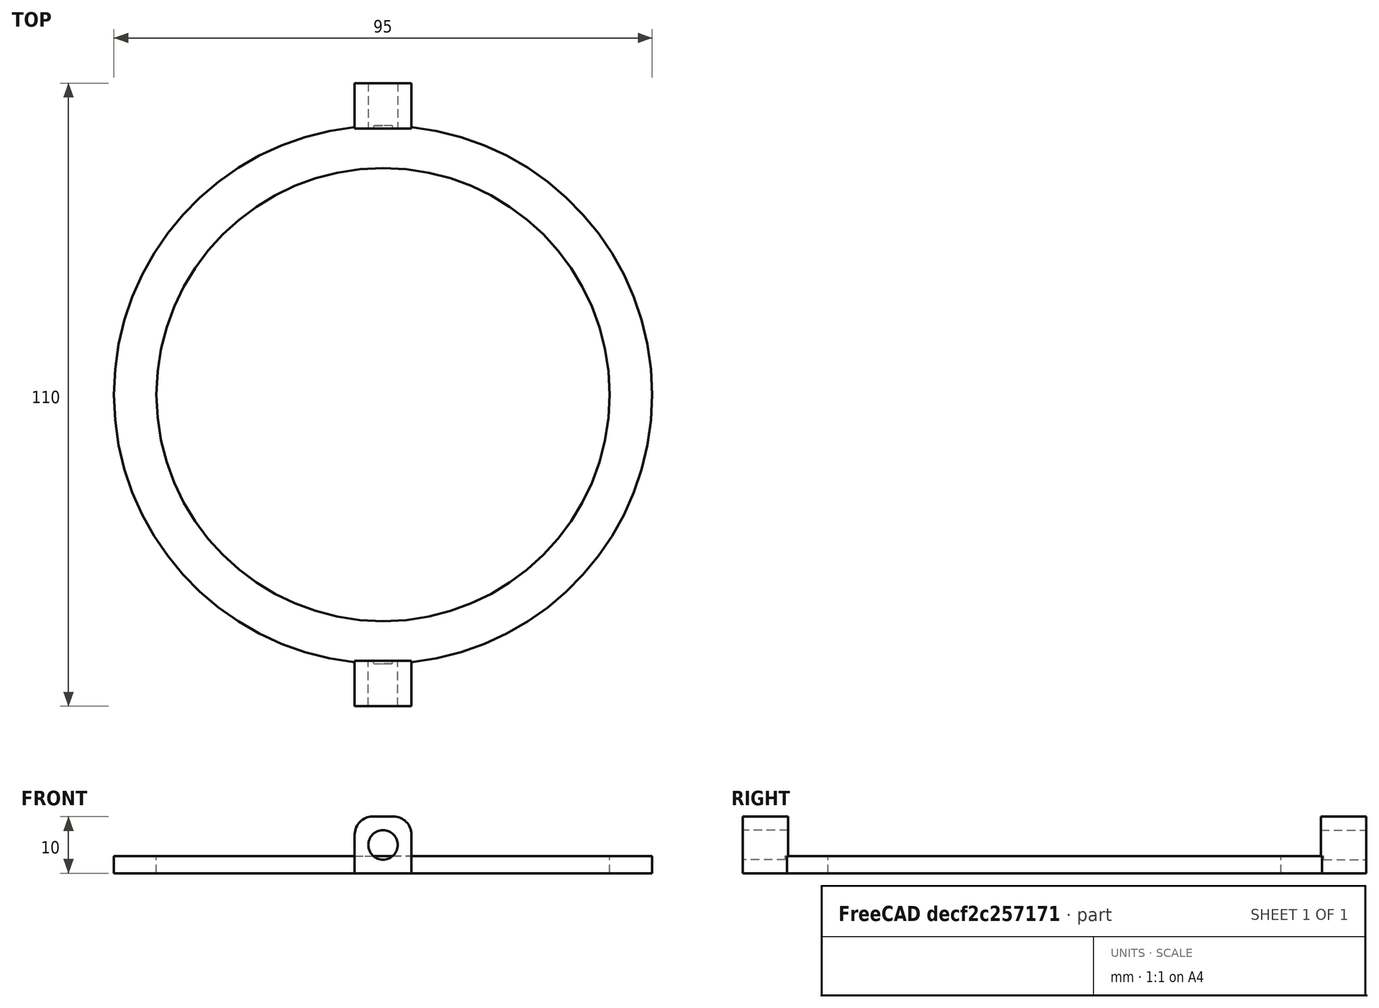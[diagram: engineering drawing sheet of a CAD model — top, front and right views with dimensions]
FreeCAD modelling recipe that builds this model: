
FCSTD DOCUMENT  (FreeCAD 0.19R24291 (Git))
Label: ring
License: All rights reserved
LicenseURL: http://en.wikipedia.org/wiki/All_rights_reserved
objects: Sketcher::SketchObject×2, PartDesign::Pad×2, PartDesign::Mirrored×2, Mesh::Feature×1, PartDesign::MultiTransform×1, PartDesign::Body×1
note: 10 computed .brp shape members not serialized (recipe doc carries the construction recipe); baked Part::Feature solids carry a one-line shape summary decoded from their .brp

FEATURE [Mesh::Feature] RING
FEATURE [Sketcher::SketchObject] Sketch
  FullyConstrained = true
  MapMode = 5
  Support = -> [XY_Plane]
  sketch-geometry (4):
    g0: ArcOfCircle CenterX=0 CenterY=0 CenterZ=0 NormalX=0 NormalY=0 NormalZ=1 AngleXU=0 Radius=40 StartAngle=0 EndAngle=1.5708
    g1: ArcOfCircle CenterX=0 CenterY=0 CenterZ=0 NormalX=0 NormalY=0 NormalZ=1 AngleXU=0 Radius=47.5 StartAngle=0 EndAngle=1.5708
    g2: LineSegment StartX=40 StartY=0 StartZ=0 EndX=47.5 EndY=0 EndZ=0
    g3: LineSegment StartX=0 StartY=40 StartZ=0 EndX=0 EndY=47.5 EndZ=0
  constraints (12):
    c: Coincident(g0,g-1)
    c: PointOnObject(g0,g-1)
    c: PointOnObject(g0,g-2)
    c: Coincident(g1,g0)
    c: PointOnObject(g1,g-1)
    c: PointOnObject(g1,g-2)
    c: Coincident(g2,g0)
    c: Coincident(g2,g1)
    c: Diameter(g0) = 80
    c: Diameter(g1) = 95
    c: Coincident(g3,g0)
    c: Coincident(g3,g1)
FEATURE [Sketcher::SketchObject] Sketch001
  AttachmentOffset = pos=(0,0,47) rot=(0,0,1;0rad)
  FullyConstrained = true
  MapMode = 5
  Placement = pos=(0,47,-1.04e-14) rot=(0,0.707107,0.707107;3.14159rad)
  Support = -> [XZ_Plane]
  sketch-geometry (7):
    g0: LineSegment StartX=0 StartY=10 StartZ=0 EndX=-1.83848 EndY=10 EndZ=0
    g1: LineSegment StartX=-5 StartY=6.83848 StartZ=0 EndX=-5 EndY=0 EndZ=0
    g2: LineSegment StartX=-5 StartY=0 StartZ=0 EndX=0 EndY=0 EndZ=0
    g3: LineSegment StartX=0 StartY=0 StartZ=0 EndX=0 EndY=2.4 EndZ=0
    g4: ArcOfCircle CenterX=0 CenterY=5 CenterZ=0 NormalX=0 NormalY=0 NormalZ=1 AngleXU=0 Radius=2.6 StartAngle=1.5708 EndAngle=4.71239
    g5: LineSegment StartX=-7.6e-14 StartY=7.6 StartZ=0 EndX=0 EndY=10 EndZ=0
    g6: ArcOfCircle CenterX=-1.83848 CenterY=6.83848 CenterZ=0 NormalX=0 NormalY=0 NormalZ=1 AngleXU=0 Radius=3.16152 StartAngle=1.5708 EndAngle=3.14159
  constraints (20):
    c: Coincident(g1,g2)
    c: Coincident(g2,g3)
    c: Coincident(g5,g0)
    c: Horizontal(g0)
    c: Horizontal(g2)
    c: Vertical(g1)
    c: Vertical(g3)
    c: PointOnObject(g0,g-2)
    c: PointOnObject(g1,g-1)
    c: PointOnObject(g4,g3)
    c: Coincident(g3,g4)
    c: Coincident(g5,g4)
    c: Tangent(g3,g5)
    c: Equal(g3,g5)
    c: Distance(g3,g4) = 5.2
    c: Distance(g2) = 5
    c: Distance(g2,g0) = 10
    c: Tangent(g1,g6) = -1.5708
    c: Tangent(g0,g6) = -1.5708
    c: PointOnObject(g6,g4)
FEATURE [PartDesign::Pad] Pad
  Direction = (1,1,1)
  Length = 3
  Length2 = 100
  Profile = -> Sketch
  Type = 0
FEATURE [PartDesign::Pad] Pad001
  BaseFeature = -> Pad
  Direction = (1,1,1)
  Length = 8
  Length2 = 100
  Profile = -> Sketch001
  Type = 0
FEATURE [PartDesign::Mirrored] Mirrored
  MirrorPlane = -> Sketch [V_Axis]
FEATURE [PartDesign::Mirrored] Mirrored001
  MirrorPlane = -> Sketch [H_Axis]
FEATURE [PartDesign::MultiTransform] MultiTransform
  BaseFeature = -> Pad001
  Originals = -> [Pad,Pad001]
  Transformations = -> [Mirrored,Mirrored001]
FEATURE [PartDesign::Body] Body
  Group = -> [Sketch,Sketch001,Pad,Pad001,MultiTransform,Mirrored,Mirrored001]
  Origin = -> Origin
  Tip = -> MultiTransform
